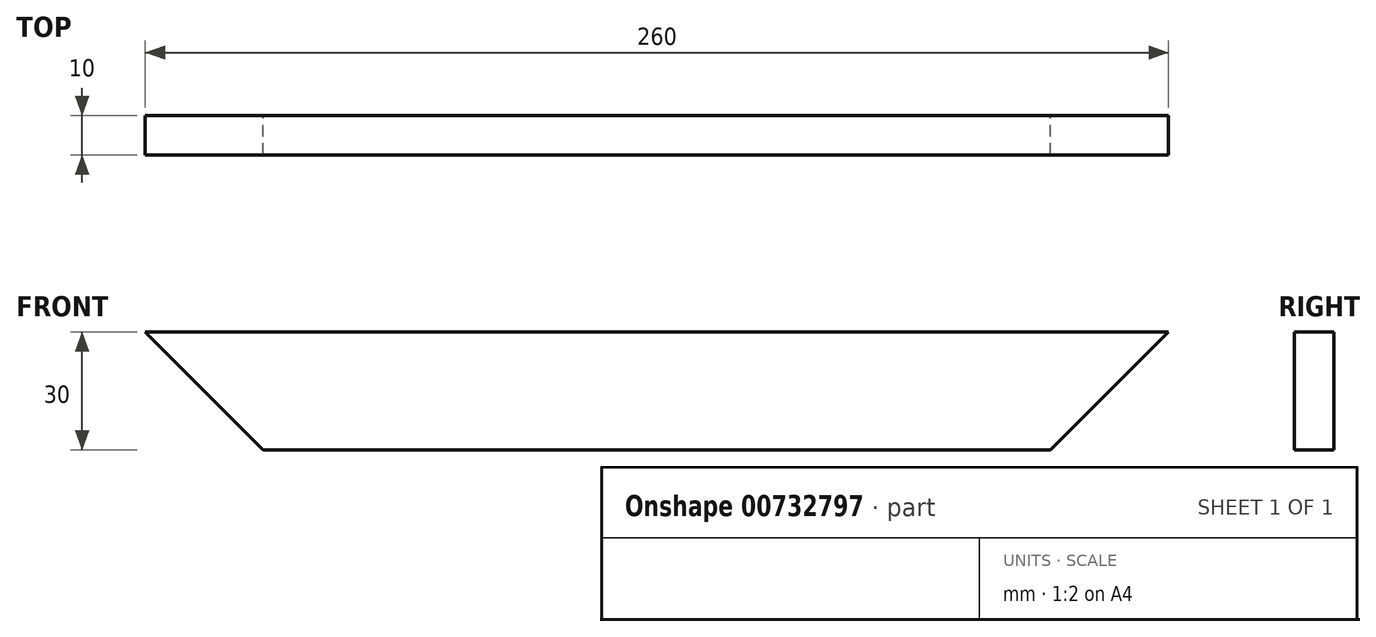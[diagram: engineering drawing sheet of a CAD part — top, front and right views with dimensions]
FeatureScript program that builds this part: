
annotation { "Feature Type Name" : "Feature", "Feature Type Description" : "" }
export const myFeature = defineFeature(function(context is Context, id is Id, definition is map)
    precondition{}
    {
        {
            var Q0;
            Q0=qCreatedBy(makeId("Front.planeOp"),FACE);
            var sketch = newSketch(context, id + "F0", { "sketchPlane" : qUnion([Q0])});
            skLineSegment(sketch, "E0", {"start": v(-23.31, -12.27) * mm, "end": v(176.69, -12.27) * mm});
            skLineSegment(sketch, "E1", {"start": v(176.69, -12.27) * mm, "end": v(206.69, 17.73) * mm});
            skLineSegment(sketch, "E2", {"start": v(206.69, 17.73) * mm, "end": v(-53.31, 17.73) * mm});
            skLineSegment(sketch, "E3", {"start": v(-53.31, 17.73) * mm, "end": v(-23.31, -12.27) * mm});
            skLineSegment(sketch, "E4", {"start": v(-23.31, -12.27) * mm, "end": v(-23.31, 17.73) * mm, "construction": true});
            skLineSegment(sketch, "E5", {"start": v(176.69, -12.27) * mm, "end": v(176.69, 17.73) * mm, "construction": true});
            skSolve(sketch);
        }
        {
            var Q0;
            Q0 = qSketchRegion(id + "F0", true);
            extrude(context, id + "F1", {"entities" : qUnion([Q0]), "depth" : 10 * mm, "offsetDistance" : 25 * mm});
        }
    });
